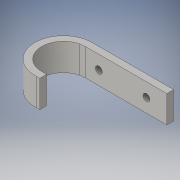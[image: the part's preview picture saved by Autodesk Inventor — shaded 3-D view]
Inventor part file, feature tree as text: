
AUTODESK INVENTOR PART (.ipt)
format: ipt  version: 2016 (Build 200138000, 138)  size: 119,808 bytes
history: native  units: in
note: dims shown in document units (in); Inventor stores cm internally (conversion verified against a paired STEP export)
features: extrude x2, sketch x2
ambient origin geometry x8: Origin, YZ Plane, XZ Plane, XY Plane, X Axis, Y Axis, Z Axis, Center Point
bodies: Solid1 (feature_tree)
feature tree (4):
  extrude  "Extrusion1"  Depth=0.25in
  extrude  "Extrusion2"  Depth=0.25in
  sketch  "Sketch1"  dims[d5=0.25in d6=3.0in]
  sketch  "Sketch2"  dims[d7=3.0in d10=1.9994in d11=0.7421in d12=0.25in d13=0.125in d15=1.0in d16=0.0in d17=0.25in d18=0.25in d19=0.75in d20=2.5in d21=0.25in d22=0.0in]
